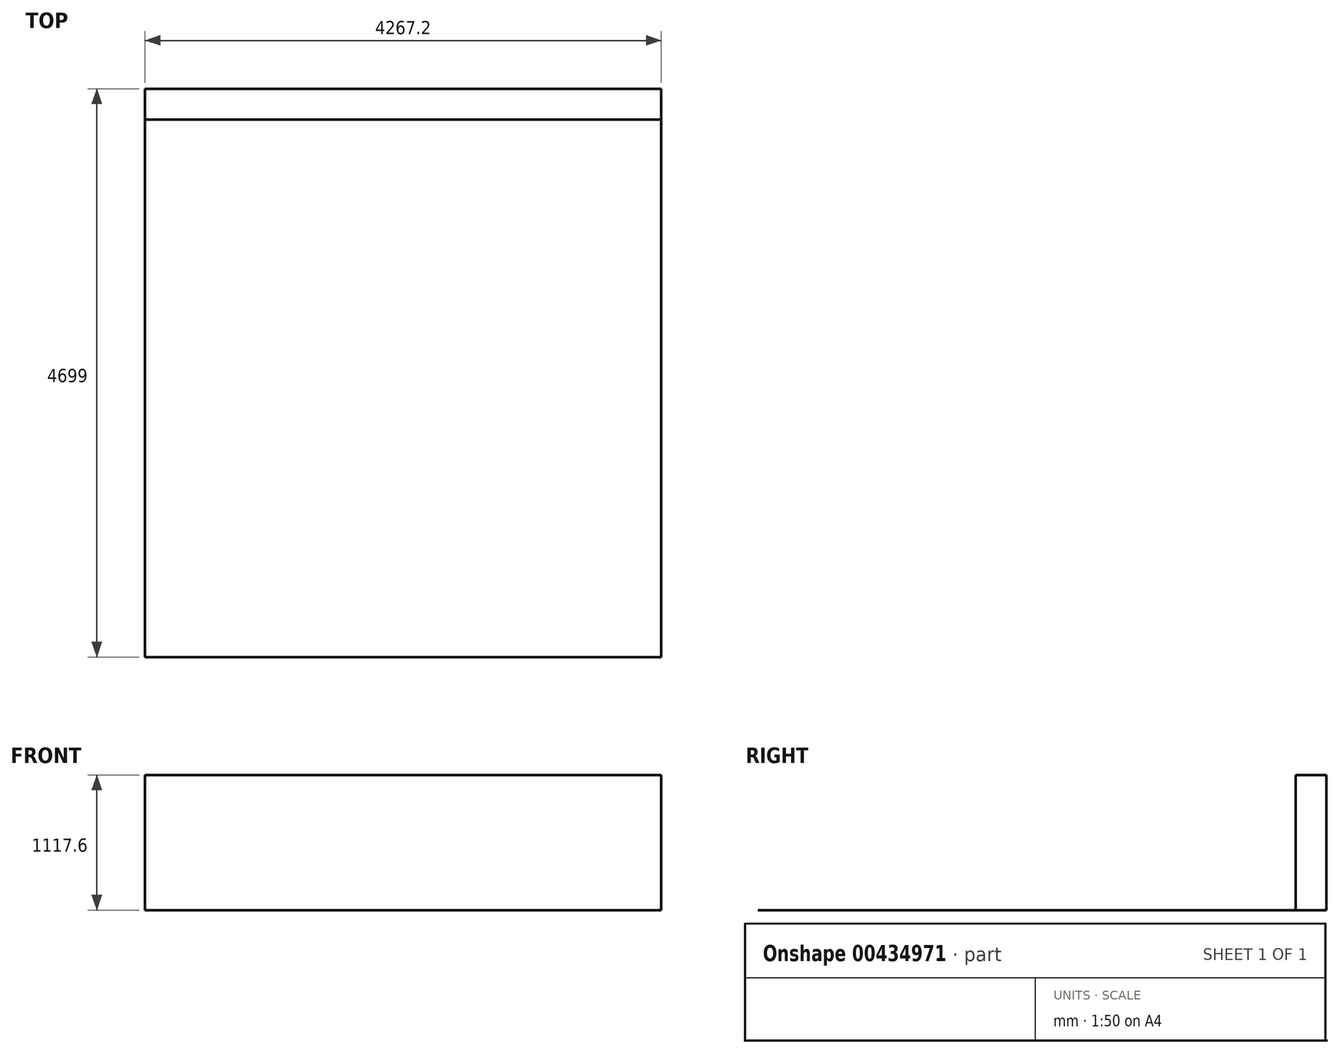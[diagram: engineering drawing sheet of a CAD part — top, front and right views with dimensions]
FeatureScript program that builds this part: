
annotation { "Feature Type Name" : "Feature", "Feature Type Description" : "" }
export const myFeature = defineFeature(function(context is Context, id is Id, definition is map)
    precondition{}
    {
        {
            var Q0;
            Q0=qCreatedBy(makeId("Front.planeOp"),FACE);
            var sketch = newSketch(context, id + "F0", { "sketchPlane" : qUnion([Q0])});
            skLineSegment(sketch, "E0.bottom", {"start": v(0, 0) * mm, "end": v(4267.2, 0) * mm});
            skLineSegment(sketch, "E0.top", {"start": v(0, 1117.6) * mm, "end": v(4267.2, 1117.6) * mm});
            skLineSegment(sketch, "E0.left", {"start": v(0, 0) * mm, "end": v(0, 1117.6) * mm});
            skLineSegment(sketch, "E0.right", {"start": v(4267.2, 0) * mm, "end": v(4267.2, 1117.6) * mm});
            skSolve(sketch);
        }
        {
            var Q0;
            Q0 = qSketchRegion(id + "F0", true);
            extrude(context, id + "F1", {"entities" : qUnion([Q0]), "oppositeDirection" : true, "depth" : 254 * mm});
        }
        {
            var Q0;
            Q0=qCreatedBy(makeId("Top.planeOp"),FACE);
            var sketch = newSketch(context, id + "F2", { "sketchPlane" : qUnion([Q0])});
            skLineSegment(sketch, "E1.bottom", {"start": v(0, 0) * mm, "end": v(4267.2, 0) * mm});
            skLineSegment(sketch, "E1.top", {"start": v(0, -4445) * mm, "end": v(4267.2, -4445) * mm});
            skLineSegment(sketch, "E1.left", {"start": v(0, 0) * mm, "end": v(0, -4445) * mm});
            skLineSegment(sketch, "E1.right", {"start": v(4267.2, 0) * mm, "end": v(4267.2, -4445) * mm});
            skSolve(sketch);
        }
        {
            var Q0;
            Q0 = qSketchRegion(id + "F2", true);
            extrude(context, id + "F3", {"entities" : qUnion([Q0]), "operationType" : NewBodyOperationType.ADD, "depth" : 0.03 * mm});
        }
    });
